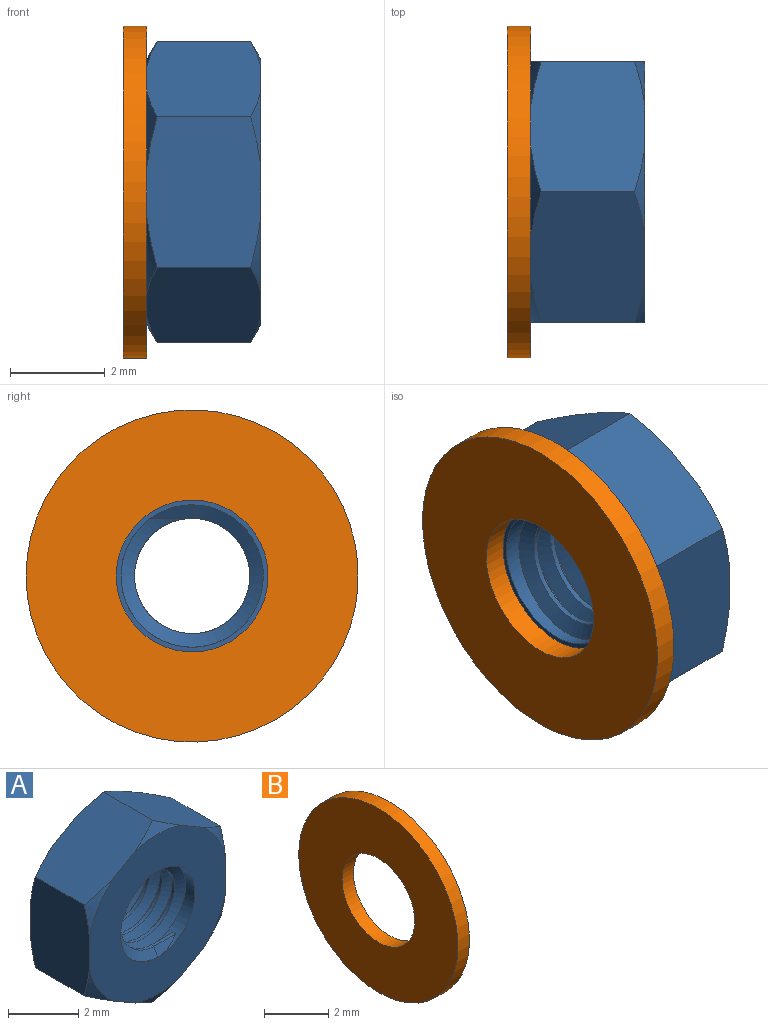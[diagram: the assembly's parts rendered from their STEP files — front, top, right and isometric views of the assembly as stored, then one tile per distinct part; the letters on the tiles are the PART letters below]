
ASSEMBLY  parts=2 mates=1
PART A: 28 faces, bbox 6.4x2.6x6.5 mm
  f0: cone r=2.8mm half-angle=60deg, axis (0,-1,0), area 0.4mm2, adj f11,f22,f23
  f1: cone r=2.8mm half-angle=60deg, axis (0,-1,0), area 0.4mm2, adj f11,f23,f24
  f2: cone r=2.8mm half-angle=60deg, axis (0,-1,0), area 0.4mm2, adj f11,f24,f25
  f3: cone r=2.8mm half-angle=60deg, axis (0,-1,0), area 0.4mm2, adj f11,f25,f26
  f4: cone r=2.8mm half-angle=60deg, axis (0,-1,0), area 0.4mm2, adj f11,f22,f27
  f5: cone r=3.18mm half-angle=60deg, axis (0,1,0), area 0.4mm2, adj f10,f22,f23
  f6: cone r=3.18mm half-angle=60deg, axis (0,1,0), area 0.4mm2, adj f10,f23,f24
  f7: cone r=3.18mm half-angle=60deg, axis (0,1,0), area 0.4mm2, adj f10,f24,f25
  f8: cone r=3.18mm half-angle=60deg, axis (0,1,0), area 0.4mm2, adj f10,f25,f26
  f9: cone r=3.18mm half-angle=60deg, axis (0,1,0), area 0.4mm2, adj f10,f26,f27
  f10: plane 5.6x5.5mm, normal (0,-1,0), area 17.4mm2, adj f5,f6,f7,f8,f9,f12,f21,f22
  f11: plane 5.6x5.5mm, normal (0,1,0), area 17.4mm2, adj f0,f1,f2,f3,f4,f12,f20,f22
  f12: cylinder r=1.5mm len=3mm, axis (0,1,0), area 6mm2, adj f10,f11,f13,f15,f16,f17,f18,f19
  f13: plane 0.44x0.25mm, normal (-0.88,0,-0.48), area 0.1mm2, adj f12,f14,f15,f16
  f14: cylinder r=1.21mm len=2.43mm, axis (0,1,0), area 3.3mm2, adj f13,f15,f16,f17
  f15: bspline ~3.46x3mm, area 11mm2, adj f12,f13,f14,f18
  f16: bspline ~3.46x3mm, area 11mm2, adj f12,f13,f14,f19
  f17: plane 0.88x0.11mm, normal (0,0,1), area 0.1mm2, adj f12,f14,f18,f19
  f18: plane 0.96x0.37mm, normal (0,0.87,0.5), area 0.2mm2, adj f12,f15,f17
  f19: plane 0.96x0.37mm, normal (0,-0.87,0.5), area 0.2mm2, adj f12,f16,f17
  f20: cone r=2.8mm half-angle=60deg, axis (0,-1,0), area 0.4mm2, adj f11,f26,f27
  f21: cone r=3.18mm half-angle=60deg, axis (0,1,0), area 0.4mm2, adj f10,f22,f27
  f22: plane 2.87x2.52mm, normal (-0.5,0,0.87), area 7.2mm2, adj f0,f4,f5,f10,f11,f21,f23,f27
  f23: plane 2.87x2.52mm, normal (0.5,0,0.87), area 7.2mm2, adj f0,f1,f5,f6,f10,f11,f22,f24
  f24: plane 3.3x2.52mm, normal (1,0,0), area 7.2mm2, adj f1,f2,f6,f7,f10,f11,f23,f25
  f25: plane 2.87x2.52mm, normal (0.5,0,-0.87), area 7.2mm2, adj f2,f3,f7,f8,f10,f11,f24,f26
  f26: plane 2.87x2.52mm, normal (-0.5,0,-0.87), area 7.2mm2, adj f3,f8,f9,f10,f11,f20,f25,f27
  f27: plane 3.3x2.52mm, normal (-1,0,0), area 7.2mm2, adj f4,f9,f10,f11,f20,f21,f22,f26
PART B: 4 faces, bbox 0.5x7x7 mm
  f0: plane 7x7mm, normal (-1,0,0), area 30.4mm2, adj f1,f3
  f1: cylinder r=1.6mm len=3.2mm, axis (1,0,0), area 5mm2, adj f0,f2
  f2: plane 7x7mm, normal (1,0,0), area 30.4mm2, adj f1,f3
  f3: cylinder r=3.5mm len=7mm, axis (1,0,0), area 11mm2, adj f0,f2
PLACE A rot(axis=(0.71,0.71,0),180deg) t=(2.9,0,0)mm
PLACE B at identity fixed
MATE fastened A.f0 <-> B.f1  axis (1,0,0) through (0.5,0,0)mm
